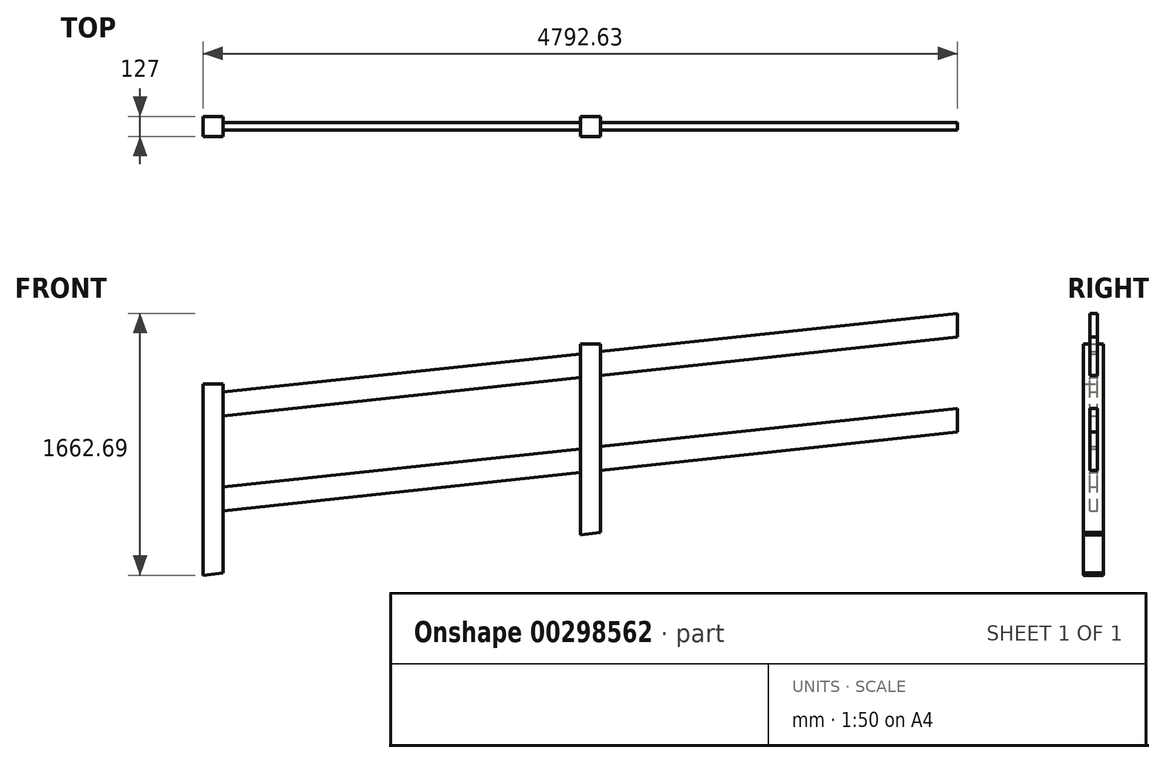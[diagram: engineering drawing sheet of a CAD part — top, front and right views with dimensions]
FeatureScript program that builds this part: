
annotation { "Feature Type Name" : "Feature", "Feature Type Description" : "" }
export const myFeature = defineFeature(function(context is Context, id is Id, definition is map)
    precondition{}
    {
        {
            var Q0;
            Q0=qCreatedBy(makeId("Front.planeOp"),FACE);
            var sketch = newSketch(context, id + "F0", { "sketchPlane" : qUnion([Q0])});
            skLineSegment(sketch, "E0", {"start": v(-16359.91, 1077.24) * mm, "end": v(-16359.91, 3696.97) * mm});
            skLineSegment(sketch, "E1", {"start": v(16340.09, 2284.03) * mm, "end": v(16340.09, 1084.03) * mm});
            skLineSegment(sketch, "E2", {"start": v(-16359.91, 1077.24) * mm, "end": v(-16518.63, -7671.73) * mm});
            skLineSegment(sketch, "E3", {"start": v(11420.46, 557.47) * mm, "end": v(11547.46, 571.06) * mm});
            skLineSegment(sketch, "E4", {"start": v(16340.09, 1084.03) * mm, "end": v(16340.09, 2284.03) * mm});
            skLineSegment(sketch, "E5", {"start": v(16340.09, 2284.03) * mm, "end": v(16213.09, 2284.03) * mm});
            skLineSegment(sketch, "E6", {"start": v(16213.09, 2284.03) * mm, "end": v(16213.09, 1070.44) * mm});
            skLineSegment(sketch, "E7", {"start": v(13943.77, 827.55) * mm, "end": v(13943.77, 2027.55) * mm});
            skLineSegment(sketch, "E8", {"start": v(13943.77, 2027.55) * mm, "end": v(13816.77, 2027.55) * mm});
            skLineSegment(sketch, "E9", {"start": v(13816.77, 2027.55) * mm, "end": v(13816.77, 813.96) * mm});
            skLineSegment(sketch, "E10", {"start": v(11547.46, 571.06) * mm, "end": v(11547.46, 1771.06) * mm});
            skLineSegment(sketch, "E11", {"start": v(11547.46, 1771.06) * mm, "end": v(11420.46, 1771.06) * mm});
            skLineSegment(sketch, "E12", {"start": v(11420.46, 1771.06) * mm, "end": v(11420.46, 557.47) * mm});
            skLineSegment(sketch, "E13", {"start": v(11547.46, 1720.78) * mm, "end": v(13816.77, 1963.67) * mm});
            skLineSegment(sketch, "E14", {"start": v(11547.46, 1569.92) * mm, "end": v(13816.77, 1812.81) * mm});
            skLineSegment(sketch, "E15", {"start": v(11547.46, 1117.35) * mm, "end": v(13816.77, 1360.24) * mm});
            skLineSegment(sketch, "E16", {"start": v(11547.46, 966.5) * mm, "end": v(13816.77, 1209.39) * mm});
            skPoint(sketch, "E17.orphan", {"position": v(16340.09, 3151.58) * mm});
            skPoint(sketch, "E18.end.orphan", {"position": v(16276.59, 2284.03) * mm});
            skPoint(sketch, "E19.orphan", {"position": v(13880.27, 2027.55) * mm});
            skLineSegment(sketch, "E20.trimOffspring", {"start": v(13943.77, 1977.26) * mm, "end": v(16213.09, 2220.16) * mm});
            skLineSegment(sketch, "E21.trimOffspring", {"start": v(13943.77, 1826.4) * mm, "end": v(16213.09, 2069.3) * mm});
            skLineSegment(sketch, "E22.trimOffspring", {"start": v(13943.77, 1222.98) * mm, "end": v(16213.09, 1465.87) * mm});
            skLineSegment(sketch, "E23.trimOffspring", {"start": v(13943.77, 1373.84) * mm, "end": v(16213.09, 1616.73) * mm});
            skPoint(sketch, "E24.start.orphan", {"position": v(11483.96, 1771.06) * mm});
            skLineSegment(sketch, "E25.trimOffspring", {"start": v(13816.77, 813.96) * mm, "end": v(13943.77, 827.55) * mm});
            skLineSegment(sketch, "E26.trimOffspring", {"start": v(16213.09, 1070.44) * mm, "end": v(16340.09, 1084.03) * mm});
            skPoint(sketch, "E27.orphan", {"position": v(-16423.4, -2422.76) * mm});
            skSolve(sketch);
        }
        {
            var Q0;
            {var subQ3=sQuery(id+"F0.wireOp",EDGE,"E3");Q0=makeQuery(id+"F0.imprint","IMPRINT",FACE,{"disambiguationData":[TD([[makeQuery(id+"F0.imprint","IMPRINT",EDGE,{"derivedFrom":subQ3}),1.0]])]});}
            var Q1;
            Q1=makeQuery(id+"F0.imprint","IMPRINT",FACE,{"disambiguationData":[TD([[makeQuery(id+"F0.imprint","IMPRINT",EDGE,{"derivedFrom":sQuery(id+"F0.wireOp",EDGE,"E4")}),1.0]])]});
            var Q2;
            {var subQ5=sQuery(id+"F0.wireOp",EDGE,"E8");Q2=makeQuery(id+"F0.imprint","IMPRINT",FACE,{"disambiguationData":[TD([[makeQuery(id+"F0.imprint","IMPRINT",EDGE,{"derivedFrom":subQ5}),1.0]])]});}
            extrude(context, id + "F1", {"entities" : qUnion([Q0, Q1, Q2]), "depth" : 63.5 * mm, "hasSecondDirection" : true, "secondDirectionOppositeDirection" : true, "secondDirectionDepth" : 63.5 * mm});
        }
        {
            var Q0;
            {var subQ0=sQuery(id+"F0.wireOp",EDGE,"E13");Q0=makeQuery(id+"F0.imprint","IMPRINT",FACE,{"disambiguationData":[TD([[makeQuery(id+"F0.imprint","IMPRINT",EDGE,{"derivedFrom":subQ0}),-1.0]])]});}
            var Q1;
            {var subQ0=sQuery(id+"F0.wireOp",EDGE,"E15");Q1=makeQuery(id+"F0.imprint","IMPRINT",FACE,{"disambiguationData":[TD([[makeQuery(id+"F0.imprint","IMPRINT",EDGE,{"derivedFrom":subQ0}),-1.0]])]});}
            var Q2;
            {var subQ0=sQuery(id+"F0.wireOp",EDGE,"E22.trimOffspring");Q2=makeQuery(id+"F0.imprint","IMPRINT",FACE,{"disambiguationData":[TD([[makeQuery(id+"F0.imprint","IMPRINT",EDGE,{"derivedFrom":subQ0}),1.0]])]});}
            var Q3;
            {var subQ0=sQuery(id+"F0.wireOp",EDGE,"E20.trimOffspring");Q3=makeQuery(id+"F0.imprint","IMPRINT",FACE,{"disambiguationData":[TD([[makeQuery(id+"F0.imprint","IMPRINT",EDGE,{"derivedFrom":subQ0}),-1.0]])]});}
            extrude(context, id + "F2", {"entities" : qUnion([Q0, Q1, Q2, Q3]), "depth" : 25 * mm, "hasSecondDirection" : true, "secondDirectionOppositeDirection" : true, "secondDirectionDepth" : 25 * mm});
        }
    });
